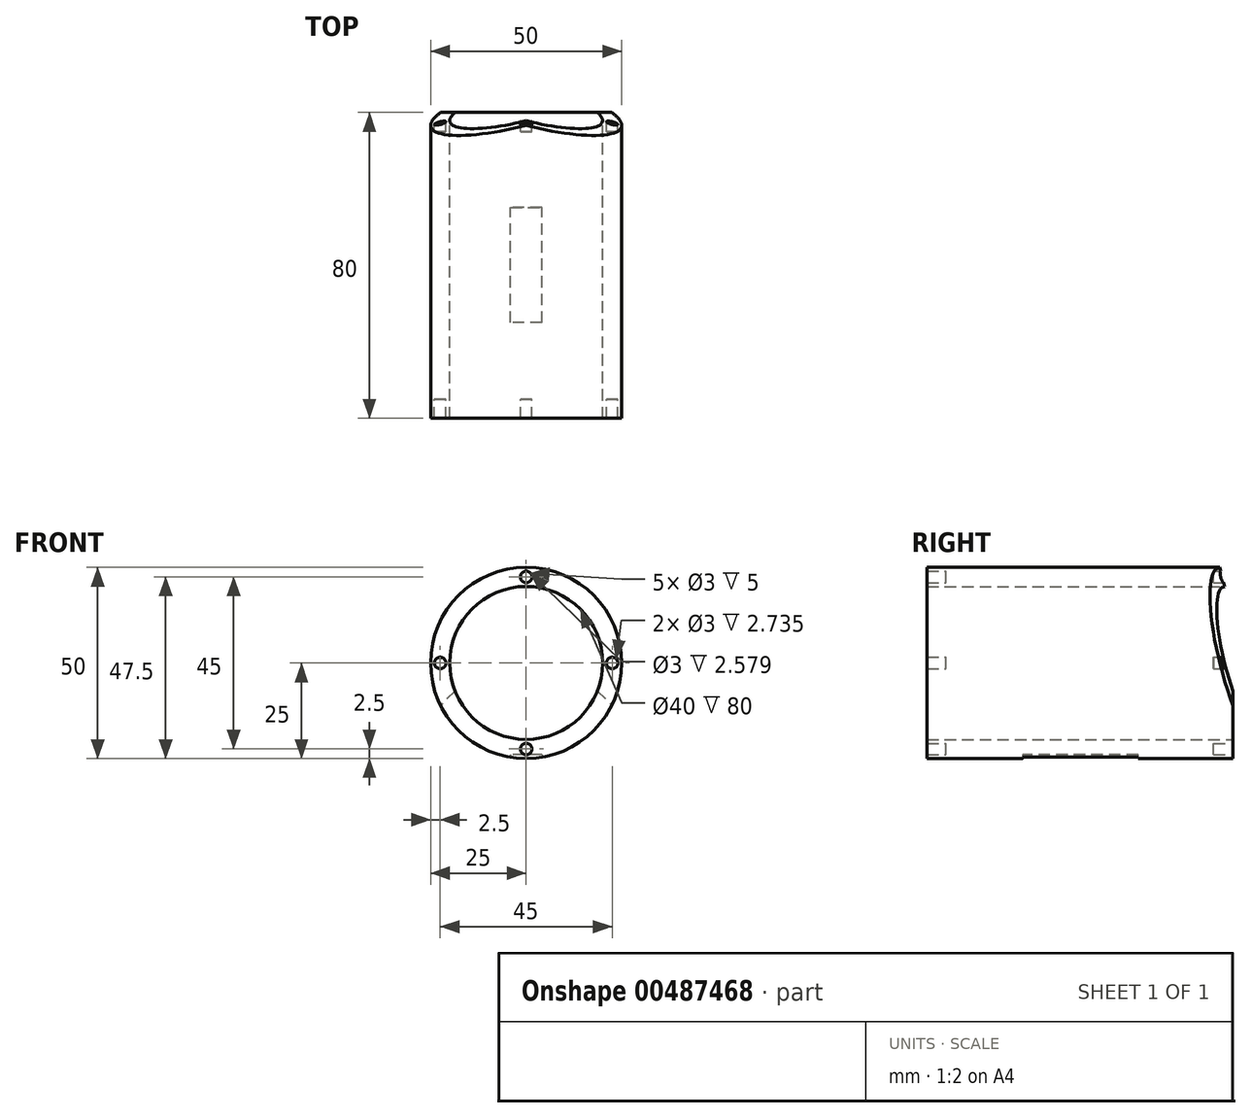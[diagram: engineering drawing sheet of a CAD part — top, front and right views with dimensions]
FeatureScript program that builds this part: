
annotation { "Feature Type Name" : "Feature", "Feature Type Description" : "" }
export const myFeature = defineFeature(function(context is Context, id is Id, definition is map)
    precondition{}
    {
        {
            var Q0;
            Q0=qCreatedBy(makeId("Front.planeOp"),FACE);
            var sketch = newSketch(context, id + "F0", { "sketchPlane" : qUnion([Q0])});
            skCircle(sketch, "E0", {"center": v(0, 0) * mm, "radius": 20 * mm});
            skCircle(sketch, "E1", {"center": v(0, 0) * mm, "radius": 25 * mm});
            skSolve(sketch);
        }
        {
            var Q0;
            Q0=qCreatedBy(makeId("Top.planeOp"),FACE);
            var sketch = newSketch(context, id + "F1", { "sketchPlane" : qUnion([Q0])});
            skLineSegment(sketch, "E2", {"start": v(0, 75.2) * mm, "end": v(0, 9.27) * mm, "construction": true});
            skSolve(sketch);
        }
        {
            var Q0;
            Q0=sQuery(id+"F1.wireOp",EDGE,"E2");
            cPlane(context, id + "F2", {"entities" : qUnion([Q0]), "cplaneType" : CPlaneType.LINE_ANGLE, "offset" : 25 * mm, "angle" : 45 * degree, "width" : 150 * mm, "height" : 150 * mm});
        }
        {
            var Q0;
            Q0=sQuery(id+"F1.wireOp",EDGE,"E2");
            cPlane(context, id + "F3", {"entities" : qUnion([Q0]), "cplaneType" : CPlaneType.LINE_ANGLE, "offset" : 25 * mm, "angle" : 45 * degree, "oppositeDirection" : true, "width" : 150 * mm, "height" : 150 * mm});
        }
        {
            var Q0;
            Q0 = qSketchRegion(id + "F0", true);
            extrude(context, id + "F4", {"entities" : qUnion([Q0]), "depth" : 80 * mm});
        }
        {
            var Q0;
            Q0=qCreatedBy(makeId("Front.planeOp"),FACE);
            var sketch = newSketch(context, id + "F5", { "sketchPlane" : qUnion([Q0])});
            skCircle(sketch, "E3", {"center": v(0, 22.5) * mm, "radius": 1.5 * mm});
            skCircle(sketch, "E4.MirrorC", {"center": v(0, -22.5) * mm, "radius": 1.5 * mm});
            skCircle(sketch, "E5", {"center": v(-22.5, 0) * mm, "radius": 1.5 * mm});
            skCircle(sketch, "E6.MirrorC", {"center": v(22.5, 0) * mm, "radius": 1.5 * mm});
            skSolve(sketch);
        }
        {
            var Q0;
            Q0 = qSketchRegion(id + "F5", true);
            extrude(context, id + "F6", {"entities" : qUnion([Q0]), "operationType" : NewBodyOperationType.REMOVE, "depth" : 84 * mm, "hasSecondDirection" : true, "secondDirectionOppositeDirection" : true, "secondDirectionDepth" : 4 * mm});
        }
        {
            var Q0;
            Q0=qCreatedBy(id+"F2.planeOp",FACE);
            var sketch = newSketch(context, id + "F7", { "sketchPlane" : qUnion([Q0])});
            skPoint(sketch, "E7.startSnap0", {"position": v(0, 7.9) * mm});
            skLineSegment(sketch, "E8", {"start": v(0, 8) * mm, "end": v(11.31, 40) * mm});
            skLineSegment(sketch, "E9", {"start": v(11.3, 40) * mm, "end": v(0, 72) * mm});
            skLineSegment(sketch, "E10", {"start": v(0, 72) * mm, "end": v(-11.31, 40) * mm});
            skLineSegment(sketch, "E11", {"start": v(-11.3, 40) * mm, "end": v(0, 8) * mm});
            skSolve(sketch);
        }
        {
            var Q0;
            Q0 = qSketchRegion(id + "F7", true);
            extrude(context, id + "F8", {"entities" : qUnion([Q0]), "operationType" : NewBodyOperationType.REMOVE, "endBound" : BoundingType.THROUGH_ALL, "oppositeDirection" : true, "depth" : 25 * mm, "hasSecondDirection" : true, "secondDirectionOppositeDirection" : false, "secondDirectionDepth" : 25 * mm});
        }
        {
            var Q0;
            Q0=qCreatedBy(id+"F3.planeOp",FACE);
            var sketch = newSketch(context, id + "F9", { "sketchPlane" : qUnion([Q0])});
            skPoint(sketch, "E12.startSnap0", {"position": v(0, -0.34) * mm});
            skLineSegment(sketch, "E13", {"start": v(0, 8) * mm, "end": v(11.3, 40) * mm});
            skLineSegment(sketch, "E14", {"start": v(11.31, 40) * mm, "end": v(0, 72) * mm});
            skLineSegment(sketch, "E15", {"start": v(0, 72) * mm, "end": v(-11.31, 40) * mm});
            skLineSegment(sketch, "E16", {"start": v(-11.3, 40) * mm, "end": v(0, 8) * mm});
            skSolve(sketch);
        }
        {
            var Q0;
            Q0 = qSketchRegion(id + "F9", true);
            extrude(context, id + "F10", {"entities" : qUnion([Q0]), "operationType" : NewBodyOperationType.REMOVE, "endBound" : BoundingType.THROUGH_ALL, "oppositeDirection" : true, "depth" : 25 * mm, "hasSecondDirection" : true, "secondDirectionOppositeDirection" : false, "secondDirectionDepth" : 25 * mm});
        }
        {
            var Q0;
            Q0=qCreatedBy(makeId("Right.planeOp"),FACE);
            var sketch = newSketch(context, id + "F11", { "sketchPlane" : qUnion([Q0])});
            skLineSegment(sketch, "E17", {"start": v(-55, -28) * mm, "end": v(-24.8, -28) * mm});
            skLineSegment(sketch, "E18", {"start": v(-24.8, -28) * mm, "end": v(-25.94, -28.22) * mm});
            skLineSegment(sketch, "E19", {"start": v(-30, -33.13) * mm, "end": v(-30, -44) * mm});
            skLineSegment(sketch, "E20", {"start": v(-35, -49) * mm, "end": v(-45, -49) * mm});
            skLineSegment(sketch, "E21", {"start": v(-50, -44) * mm, "end": v(-50, -33.28) * mm});
            skLineSegment(sketch, "E22", {"start": v(-53.4, -28.54) * mm, "end": v(-55, -28) * mm});
            skCircle(sketch, "E23", {"center": v(-40, -39) * mm, "radius": 3.5 * mm});
            skPoint(sketch, "E24.visualSharp", {"position": v(-30, -49) * mm});
            skArc(sketch, "E24.filletArc", {"start": v(-35, -49) * mm, "mid": v(-31.46, -47.53) * mm, "end": v(-30, -44) * mm});
            skPoint(sketch, "E25.visualSharp", {"position": v(-50, -49) * mm});
            skArc(sketch, "E25.filletArc", {"start": v(-50, -44) * mm, "mid": v(-48.54, -47.53) * mm, "end": v(-45, -49) * mm});
            skPoint(sketch, "E26.visualSharp", {"position": v(-50, -29.69) * mm});
            skArc(sketch, "E26.filletArc", {"start": v(-50, -33.28) * mm, "mid": v(-50.94, -30.36) * mm, "end": v(-53.4, -28.54) * mm});
            skPoint(sketch, "E27.visualSharp", {"position": v(-30, -29) * mm});
            skArc(sketch, "E27.filletArc", {"start": v(-25.94, -28.22) * mm, "mid": v(-28.85, -29.94) * mm, "end": v(-30, -33.13) * mm});
            skLineSegment(sketch, "E28", {"start": v(-24.8, -28) * mm, "end": v(-24.8, -24) * mm});
            skLineSegment(sketch, "E29", {"start": v(-24.8, -24) * mm, "end": v(-55, -24) * mm});
            skLineSegment(sketch, "E30", {"start": v(-55, -24) * mm, "end": v(-55, -28) * mm});
            skSolve(sketch);
        }
        {
            var Q0;
            Q0=qCreatedBy(makeId("Front.planeOp"),FACE);
            var Q1;
            Q1 = qBodyType(qCreatedBy(id + "F13" ,EDGE), BodyType.WIRE);
            cPlane(context, id + "F12", {"entities" : qUnion([Q0, Q1]), "cplaneType" : CPlaneType.OFFSET, "offset" : 40 * mm, "width" : 150 * mm, "height" : 150 * mm});
        }
        {
            var Q0;
            Q0=qCreatedBy(id+"F12.planeOp",FACE);
            var sketch = newSketch(context, id + "F13", { "sketchPlane" : qUnion([Q0])});
            skCircle(sketch, "E31", {"center": v(0, 22.5) * mm, "radius": 1.5 * mm});
            skCircle(sketch, "E32.MirrorC", {"center": v(0, -22.5) * mm, "radius": 1.5 * mm});
            skCircle(sketch, "E33", {"center": v(22.5, 0) * mm, "radius": 1.5 * mm});
            skCircle(sketch, "E34.MirrorC", {"center": v(-22.5, 0) * mm, "radius": 1.5 * mm});
            skSolve(sketch);
        }
        {
            var Q0;
            Q0 = qSketchRegion(id + "F13", true);
            extrude(context, id + "F14", {"entities" : qUnion([Q0]), "operationType" : NewBodyOperationType.ADD, "depth" : 35 * mm, "hasSecondDirection" : true, "secondDirectionOppositeDirection" : true, "secondDirectionDepth" : 35 * mm});
        }
        {
            var Q0;
            Q0 = qSketchRegion(id + "F11", true);
            extrude(context, id + "F15", {"entities" : qUnion([Q0]), "operationType" : NewBodyOperationType.REMOVE, "depth" : 4.1 * mm, "hasSecondDirection" : true, "secondDirectionOppositeDirection" : true, "secondDirectionDepth" : 4.1 * mm});
        }
    });
